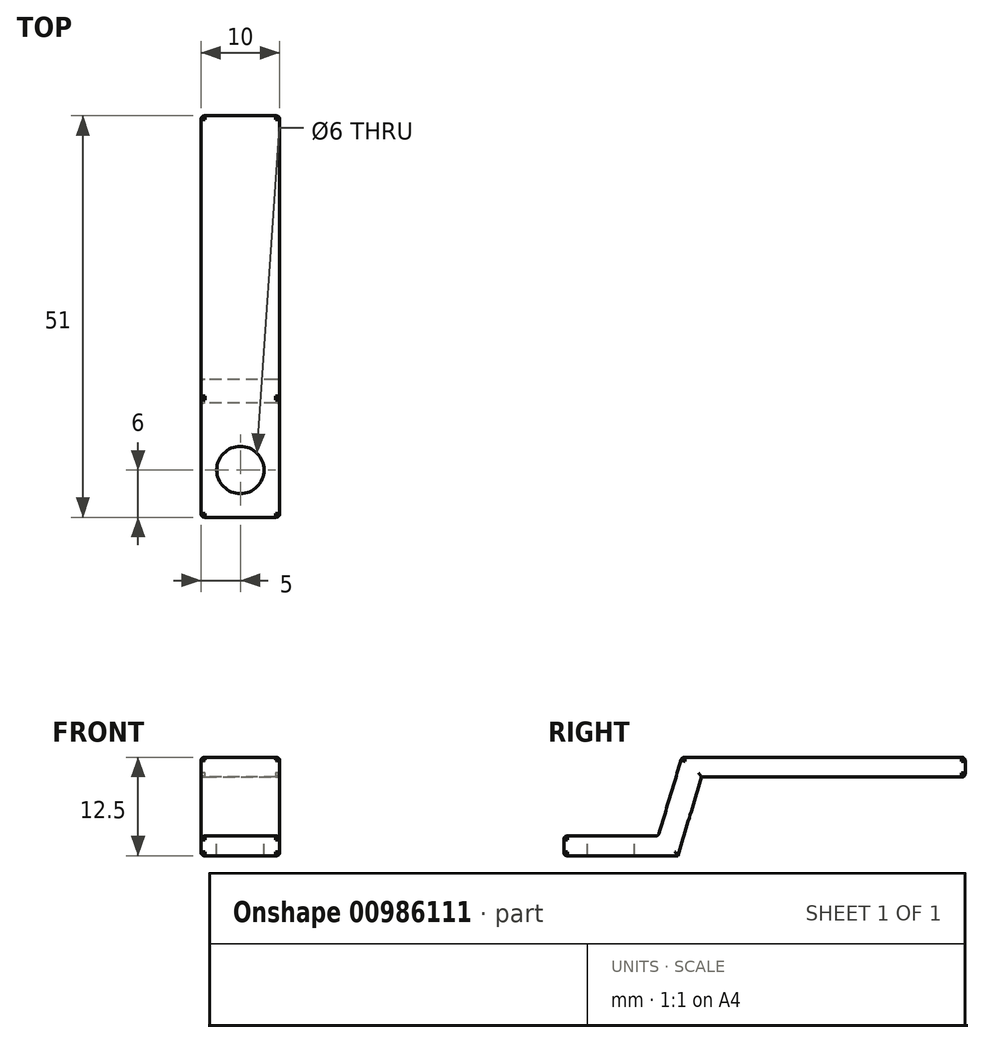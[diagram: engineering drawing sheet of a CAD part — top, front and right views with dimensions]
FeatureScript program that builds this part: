
annotation { "Feature Type Name" : "Feature", "Feature Type Description" : "" }
export const myFeature = defineFeature(function(context is Context, id is Id, definition is map)
    precondition{}
    {
        {
            var Q0;
            Q0=qCreatedBy(makeId("Right.planeOp"),FACE);
            var sketch = newSketch(context, id + "F0", { "sketchPlane" : qUnion([Q0])});
            skLineSegment(sketch, "E0", {"start": v(0, 0) * mm, "end": v(14.5, 0) * mm});
            skLineSegment(sketch, "E1", {"start": v(17.5, 10) * mm, "end": v(51, 10) * mm});
            skLineSegment(sketch, "E2", {"start": v(51, 10) * mm, "end": v(51, 12.5) * mm});
            skLineSegment(sketch, "E3", {"start": v(51, 12.5) * mm, "end": v(16, 12.5) * mm});
            skLineSegment(sketch, "E4", {"start": v(12, 2.5) * mm, "end": v(0, 2.5) * mm});
            skLineSegment(sketch, "E5", {"start": v(14.5, 0) * mm, "end": v(17.5, 10) * mm});
            skLineSegment(sketch, "E6", {"start": v(12, 2.5) * mm, "end": v(15, 12.5) * mm});
            skLineSegment(sketch, "E7", {"start": v(15, 12.5) * mm, "end": v(16, 12.5) * mm});
            skLineSegment(sketch, "E8", {"start": v(0, 2.5) * mm, "end": v(0, 0) * mm});
            skSolve(sketch);
        }
        {
            var Q0;
            Q0=makeQuery(id+"F0.imprint","IMPRINT",FACE,{"disambiguationData":[TD([[makeQuery(id+"F0.imprint","IMPRINT",EDGE,{"derivedFrom":sQuery(id+"F0.wireOp",EDGE,"E0")}),1.0]])]});
            var sketch = newSketch(context, id + "F1", { "sketchPlane" : qUnion([Q0])});
            skSolve(sketch);
        }
        {
            var Q0;
            Q0=makeQuery(id+"F1.imprint","IMPRINT",FACE,{"disambiguationData":[TD([[makeQuery(id+"F1.imprint","IMPRINT",EDGE,{"derivedFrom":makeQuery(id+"F0.imprint","IMPRINT",EDGE,{"derivedFrom":sQuery(id+"F0.wireOp",EDGE,"E0")})}),1.0]])]});
            extrude(context, id + "F2", {"entities" : qUnion([Q0]), "depth" : 5 * mm, "offsetDistance" : 25 * mm, "hasSecondDirection" : true, "secondDirectionOppositeDirection" : true, "secondDirectionDepth" : 5 * mm});
        }
        {
            var Q0;
            Q0=makeQuery(id+"F2.opExtrude","CAP_FACE",FACE,{"disambiguationData":[OSD([sQuery(id+"F0.wireOp",EDGE,"E0"),sQuery(id+"F0.wireOp",EDGE,"E1"),sQuery(id+"F0.wireOp",EDGE,"E2"),sQuery(id+"F0.wireOp",EDGE,"E3"),sQuery(id+"F0.wireOp",EDGE,"E4"),sQuery(id+"F0.wireOp",EDGE,"E5"),sQuery(id+"F0.wireOp",EDGE,"E6"),sQuery(id+"F0.wireOp",EDGE,"E7"),sQuery(id+"F0.wireOp",EDGE,"E8")])],"isStart":false});
            var Q1;
            Q1=makeQuery(id+"F2.opExtrude","SWEPT_FACE",FACE,{"disambiguationData":[OSD([sQuery(id+"F0.wireOp",EDGE,"E3"),sQuery(id+"F0.wireOp",EDGE,"E7")])]});
            var Q2;
            Q2=makeQuery(id+"F2.opExtrude","SWEPT_FACE",FACE,{"disambiguationData":[OSD([sQuery(id+"F0.wireOp",EDGE,"E6")])]});
            var Q3;
            Q3=makeQuery(id+"F2.opExtrude","SWEPT_FACE",FACE,{"disambiguationData":[OSD([sQuery(id+"F0.wireOp",EDGE,"E4")])]});
            var Q4;
            Q4=makeQuery(id+"F2.opExtrude","SWEPT_FACE",FACE,{"disambiguationData":[OSD([sQuery(id+"F0.wireOp",EDGE,"E8")])]});
            var Q5;
            Q5=makeQuery(id+"F2.opExtrude","CAP_FACE",FACE,{"disambiguationData":[OSD([sQuery(id+"F0.wireOp",EDGE,"E0"),sQuery(id+"F0.wireOp",EDGE,"E1"),sQuery(id+"F0.wireOp",EDGE,"E2"),sQuery(id+"F0.wireOp",EDGE,"E3"),sQuery(id+"F0.wireOp",EDGE,"E4"),sQuery(id+"F0.wireOp",EDGE,"E5"),sQuery(id+"F0.wireOp",EDGE,"E6"),sQuery(id+"F0.wireOp",EDGE,"E7"),sQuery(id+"F0.wireOp",EDGE,"E8")])],"isStart":true});
            var Q6;
            Q6=makeQuery(id+"F2.opExtrude","SWEPT_FACE",FACE,{"disambiguationData":[OSD([sQuery(id+"F0.wireOp",EDGE,"E2")])]});
            fillet(context, id + "F3", {"entities" : qUnion([Q0, Q1, Q2, Q3, Q4, Q5, Q6]), "radius" : 0.5 * mm, "tangentPropagation" : true, "rho" : 0.5, "crossSection" : FilletCrossSection.CONIC, "allowEdgeOverflow" : false});
        }
        {
            var Q0;
            Q0=makeQuery(id+"F2.opExtrude","SWEPT_FACE",FACE,{"disambiguationData":[OSD([sQuery(id+"F0.wireOp",EDGE,"E4")])]});
            cPlane(context, id + "F4", {"entities" : qUnion([Q0]), "cplaneType" : CPlaneType.OFFSET, "offset" : 0 * mm, "width" : 150 * mm, "height" : 150 * mm});
        }
        {
            var Q0;
            Q0=qCreatedBy(id+"F4.planeOp",FACE);
            var sketch = newSketch(context, id + "F5", { "sketchPlane" : qUnion([Q0])});
            skLineSegment(sketch, "E9", {"start": v(0, 0) * mm, "end": v(0, 6) * mm});
            skCircle(sketch, "E10", {"center": v(0, 6) * mm, "radius": 3 * mm});
            skSolve(sketch);
        }
        {
            var Q0;
            Q0=makeQuery(id+"F5.imprint","IMPRINT",FACE,{"disambiguationData":[TD([[makeQuery(id+"F5.imprint","IMPRINT",EDGE,{"derivedFrom":sQuery(id+"F5.wireOp",EDGE,"E10")}),1.0]])]});
            extrude(context, id + "F6", {"entities" : qUnion([Q0]), "operationType" : NewBodyOperationType.REMOVE, "oppositeDirection" : true, "depth" : 25 * mm, "offsetDistance" : 25 * mm});
        }
    });
